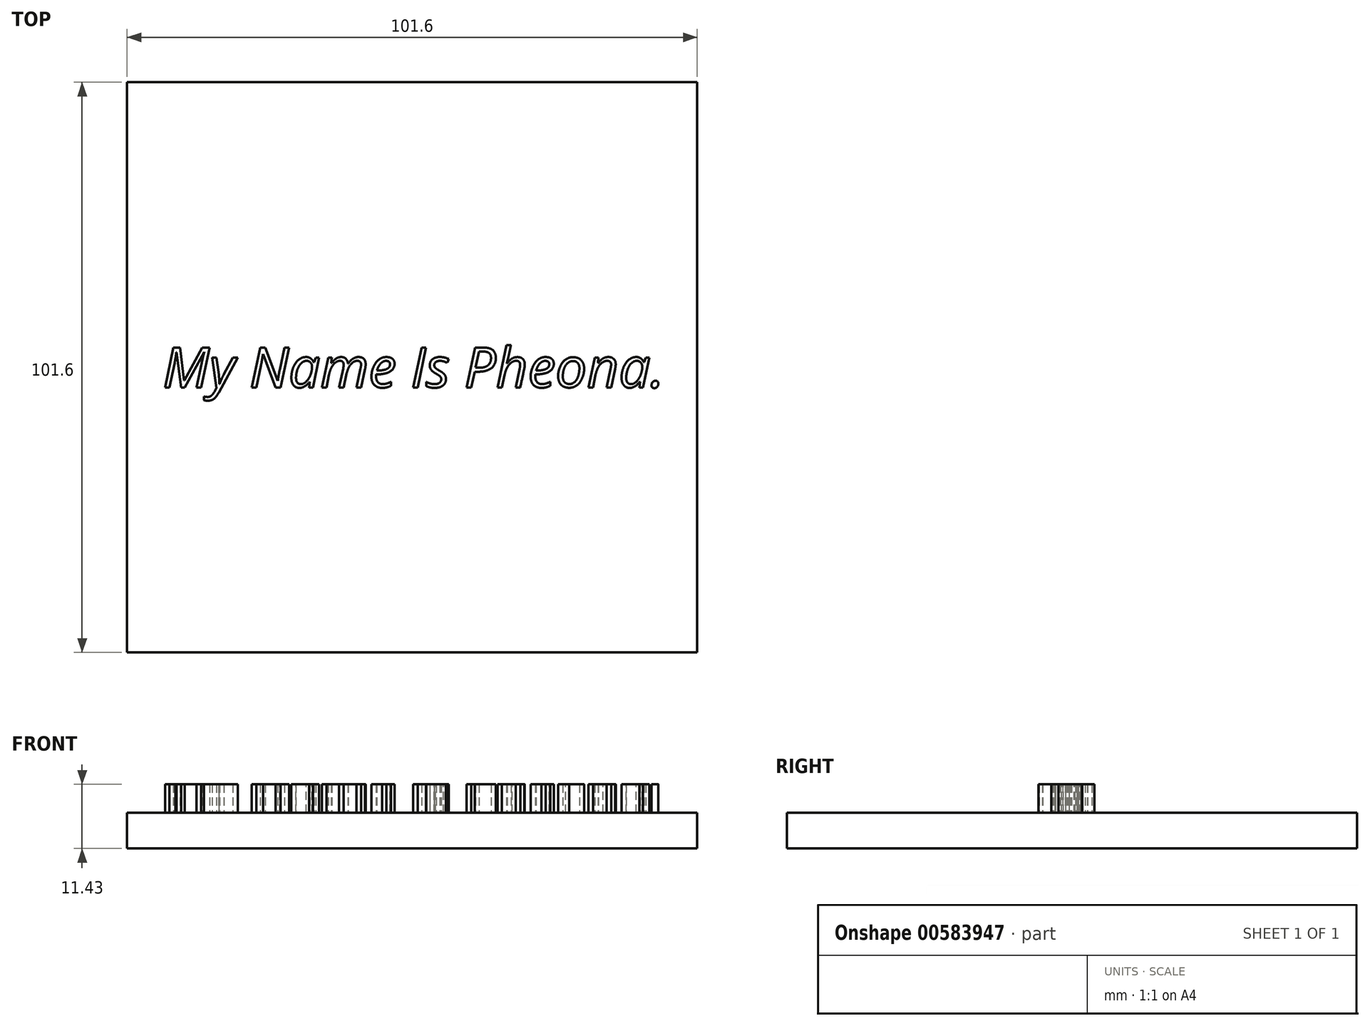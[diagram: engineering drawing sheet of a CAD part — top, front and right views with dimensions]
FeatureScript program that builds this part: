
annotation { "Feature Type Name" : "Feature", "Feature Type Description" : "" }
export const myFeature = defineFeature(function(context is Context, id is Id, definition is map)
    precondition{}
    {
        {
            var Q0;
            Q0=qCreatedBy(makeId("Top.planeOp"),FACE);
            var sketch = newSketch(context, id + "F0", { "sketchPlane" : qUnion([Q0])});
            skLineSegment(sketch, "E0.bottom", {"start": v(-50.8, 50.8) * mm, "end": v(50.8, 50.8) * mm});
            skLineSegment(sketch, "E0.top", {"start": v(-50.8, -50.8) * mm, "end": v(50.8, -50.8) * mm});
            skLineSegment(sketch, "E0.left", {"start": v(-50.8, 50.8) * mm, "end": v(-50.8, -50.8) * mm});
            skLineSegment(sketch, "E0.right", {"start": v(50.8, 50.8) * mm, "end": v(50.8, -50.8) * mm});
            skSolve(sketch);
        }
        {
            var Q0;
            Q0=makeQuery(id+"F0.imprint","IMPRINT",FACE,{"disambiguationData":[TD([[makeQuery(id+"F0.imprint","IMPRINT",EDGE,{"derivedFrom":sQuery(id+"F0.wireOp",EDGE,"E0.bottom")}),-1.0]])]});
            extrude(context, id + "F1", {"entities" : qUnion([Q0]), "depth" : 6.35 * mm, "offsetDistance" : 25.4 * mm});
        }
        {
            var Q0;
            Q0=makeQuery(id+"F1.opExtrude","CAP_FACE",FACE,{"disambiguationData":[OSD([sQuery(id+"F0.wireOp",EDGE,"E0.bottom"),sQuery(id+"F0.wireOp",EDGE,"E0.top"),sQuery(id+"F0.wireOp",EDGE,"E0.left"),sQuery(id+"F0.wireOp",EDGE,"E0.right")])],"isStart":false});
            var sketch = newSketch(context, id + "F2", { "sketchPlane" : qUnion([Q0])});
            skText(sketch, "E1", { "text": "My Name Is Pheona.", "fontName": "OpenSans-Italic.ttf"});
            const initialGuessF2  = {"E1": [-0.04445, -0.00357, 1, 0, 0.00715]};
            skSetInitialGuess(sketch, initialGuessF2);
            skSolve(sketch);
        }
        {
            var Q0;
            Q0 = qSketchRegion(id + "F2", true);
            extrude(context, id + "F3", {"entities" : qUnion([Q0]), "operationType" : NewBodyOperationType.ADD, "depth" : 5.08 * mm, "offsetDistance" : 25.4 * mm});
        }
    });
